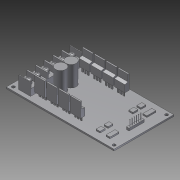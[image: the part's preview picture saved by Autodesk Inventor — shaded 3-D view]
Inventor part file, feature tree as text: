
AUTODESK INVENTOR PART (.ipt)
format: ipt  version: 2011 SP2 (Build 150309200, 309)  size: 478,208 bytes
history: native  units: mm
features: extrude x13, projected_geometry x8, sketch x7, fillet x1
ambient origin geometry x8: Origin, YZ Plane, XZ Plane, XY Plane, X Axis, Y Axis, Z Axis, Center Point
bodies: Solid1 (feature_tree)
feature tree (29):
  extrude  "Extrusion1"  Depth=54.075mm
  sketch  "Sketch2"  dims[d2=60.0mm d3=30.0mm]
  extrude  "Extrusion2"  Depth=30.0mm
  extrude  "Extrusion3"  Depth=3.0mm
  extrude  "Extrusion4"  Depth=3.0mm
  extrude  "Extrusion5"  Depth=2.15mm
  fillet  "Fillet1"  Radius=2.0mm
  extrude  "Extrusion6"  Depth=2.0mm
  extrude  "Extrusion7"  Depth=2.15mm
  extrude  "Extrusion8"  Depth=2.15mm
  extrude  "Extrusion9"  Depth=2.15mm
  extrude  "Extrusion10"  Depth=52.0mm
  extrude  "Extrusion11"  Depth=11.9mm
  extrude  "Extrusion12"  Depth=8.45mm
  extrude  "Extrusion13"  Depth=4.0mm
  sketch  "Sketch1"  dims[d0=108.15mm d1=54.075mm]
  sketch  "Sketch3"  dims[d4=1.6mm d5=0.0mm d6=3.0mm]
  projected_geometry  "Projected Loop1"
  projected_geometry  "Projected Loop2"
  projected_geometry  "Projected Loop3"
  projected_geometry  "Projected Loop4"
  projected_geometry  "Projected Loop5"
  sketch  "Sketch4"  dims[d7=3.0mm d8=3.0mm]
  projected_geometry  "Projected Loop6"
  sketch  "Sketch5"  dims[d9=3.0mm d10=2.15mm d11=2.0mm]
  projected_geometry  "Projected Loop7"
  sketch  "Sketch6"  dims[d12=2.0mm d13=2.0mm]
  projected_geometry  "Projected Loop8"
  sketch  "Sketch7"  dims[d15=2.0mm d16=2.15mm d17=2.15mm d18=2.15mm d19=52.0mm d20=11.9mm d21=8.45mm d22=4.0mm d23=0.6mm d24=0.6mm d25=2.6mm d27=43.45mm d28=8.275mm d29=4.0mm d30=5.0mm d31=21.4mm d32=15.3mm d33=2.5mm d34=25.0mm d35=15.0mm d36=7.0mm d37=7.0mm d38=46.0mm d39=4.0mm d40=9.0mm d41=7.0mm d42=7.0mm d43=3.0mm d44=3.0mm d45=8.2mm d46=1.6mm d47=0.0mm d48=1.3mm d49=1.3mm d50=1.3mm d51=0.65mm d52=1.3mm d53=1.3mm d54=0.65mm d55=7.36mm d56=7.36mm d57=7.36mm d58=7.36mm d59=7.36mm d60=12.5mm d61=0.0mm d62=6.6mm d63=0.0mm d64=5.0mm d65=5.0mm d66=5.0mm d67=5.0mm d68=5.0mm d69=5.0mm d70=4.0mm d71=0.0mm d72=2.0mm d73=4.35mm d74=0.0mm d75=4.45mm d76=1.0mm d77=1.0mm d78=4.45mm d79=14.55mm d80=0.0mm d81=6.65mm d82=105.0deg d83=1.3mm d84=105.0deg d85=1.3mm d86=14.55mm d87=0.0mm d88=10.3mm d89=1.6mm d90=1.6mm d91=1.6mm d92=10.3mm d93=10.3mm d99=1.5mm d101=1.5mm d106=1.55mm d107=1.55mm d108=1.55mm d109=1.325mm d110=1.5mm d111=1.5mm d112=1.55mm d113=1.55mm d114=1.325mm d115=1.55mm d116=1.55mm d117=1.55mm d118=1.55mm d119=1.55mm d120=1.55mm d121=1.55mm d122=1.5mm d123=1.5mm d124=1.325mm d125=1.5mm d126=1.5mm d127=1.325mm d128=53.3mm d129=0.0mm d130=2.5mm d131=0.0mm d132=2.185mm d133=2.186mm d134=2.185mm d135=2.186mm d136=2.186mm d137=2.186mm d138=0.6mm d139=0.6mm d140=0.6mm d141=0.6mm d142=0.6mm d143=0.6mm d144=5.9mm d145=0.0mm d146=1.5mm d147=0.0mm d148=4.3mm d149=4.3mm d150=10.3mm d151=10.3mm d152=10.45mm d153=24.775mm d154=20.4mm d155=0.0mm]
